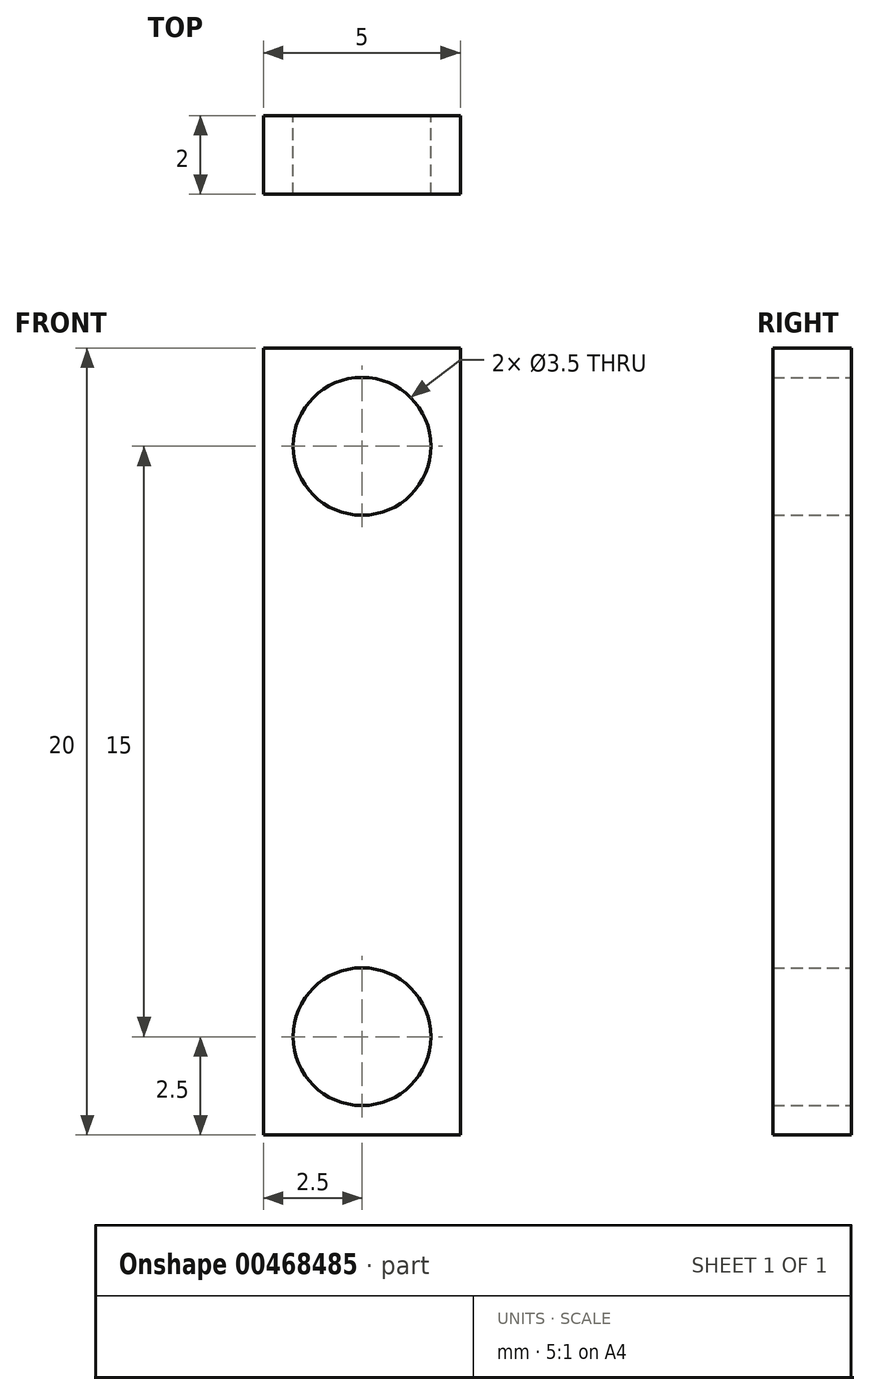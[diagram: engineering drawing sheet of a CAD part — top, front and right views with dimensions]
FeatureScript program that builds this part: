
annotation { "Feature Type Name" : "Feature", "Feature Type Description" : "" }
export const myFeature = defineFeature(function(context is Context, id is Id, definition is map)
    precondition{}
    {
        {
            var Q0;
            Q0=qCreatedBy(makeId("Front.planeOp"),FACE);
            var sketch = newSketch(context, id + "F0", { "sketchPlane" : qUnion([Q0])});
            skLineSegment(sketch, "E0", {"start": v(-12.35, 0) * mm, "end": v(12.35, 0) * mm, "construction": true});
            skLineSegment(sketch, "E1", {"start": v(0, -18.19) * mm, "end": v(0, 24.02) * mm, "construction": true});
            skLineSegment(sketch, "E2.bottom", {"start": v(-2.5, -5) * mm, "end": v(2.5, -5) * mm});
            skLineSegment(sketch, "E2.top", {"start": v(-2.5, 15) * mm, "end": v(2.5, 15) * mm});
            skLineSegment(sketch, "E2.left", {"start": v(-2.5, -5) * mm, "end": v(-2.5, 15) * mm});
            skLineSegment(sketch, "E2.right", {"start": v(2.5, -5) * mm, "end": v(2.5, 15) * mm});
            skCircle(sketch, "E3", {"center": v(0, -2.5) * mm, "radius": 1.75 * mm});
            skLineSegment(sketch, "E4", {"start": v(-3.43, 0) * mm, "end": v(-3.43, -5) * mm, "construction": true});
            skLineSegment(sketch, "E5", {"start": v(0, -2.5) * mm, "end": v(-3.43, -2.5) * mm, "construction": true});
            skLineSegment(sketch, "E6", {"start": v(2.5, 5) * mm, "end": v(-2.5, 5) * mm, "construction": true});
            skCircle(sketch, "E7.MirrorC", {"center": v(0, 12.5) * mm, "radius": 1.75 * mm});
            skSolve(sketch);
        }
        {
            var Q0;
            Q0=makeQuery(id+"F0.imprint","IMPRINT",FACE,{"disambiguationData":[TD([[makeQuery(id+"F0.imprint","IMPRINT",EDGE,{"derivedFrom":sQuery(id+"F0.wireOp",EDGE,"E2.bottom")}),1.0]])]});
            extrude(context, id + "F1", {"entities" : qUnion([Q0]), "depth" : 2 * mm});
        }
    });
